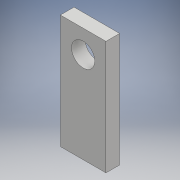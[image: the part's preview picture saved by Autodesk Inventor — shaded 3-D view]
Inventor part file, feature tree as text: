
AUTODESK INVENTOR PART (.ipt)
format: ipt  version: 2018 (Build 220112000, 112)  size: 229,376 bytes
history: native  units: mm
features: extrude x3, sketch x3
ambient origin geometry x8: Origin, YZ Plane, XZ Plane, XY Plane, X Axis, Y Axis, Z Axis, Center Point
bodies: Solid1 (feature_tree)
feature tree (6):
  extrude  "Extrusion1"  Depth=25.0mm
  extrude  "Extrusion2"  Depth=10.0mm
  extrude  "Extrusion4"  Depth=10.0mm TaperAngle=0.0deg
  sketch  "Sketch1"  dims[d0=10.0mm d1=25.0mm]
  sketch  "Sketch2"  dims[d2=10.0mm d3=0.0mm d4=5.0mm]
  sketch  "Sketch4"  dims[d5=5.1mm d6=10.0mm d7=0.0mm d13=25.0mm d14=7.0mm d15=0.0mm]
